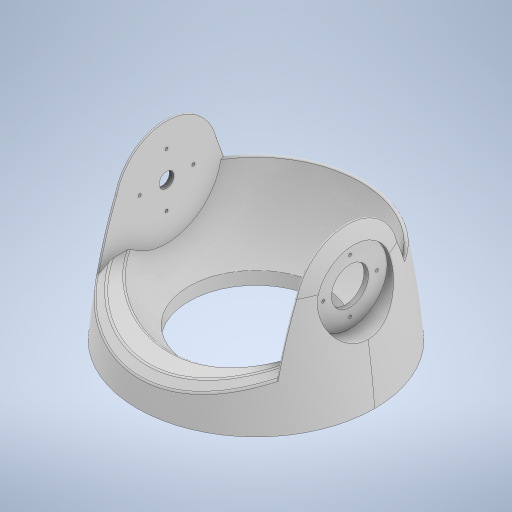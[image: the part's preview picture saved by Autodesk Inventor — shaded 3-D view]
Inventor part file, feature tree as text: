
AUTODESK INVENTOR PART (.ipt)
format: ipt  version: 2023 (Build 270158000, 158)  size: 764,416 bytes
history: native  units: mm
features: sketch x17, extrude x16, fillet x4, other x3, revolve x3, chamfer x3, mirror x2, projected_geometry x2, pattern_circular x1
ambient origin geometry x8: Origin, YZ Plane, XZ Plane, XY Plane, X Axis, Y Axis, Z Axis, Center Point
bodies: Body1 (feature_tree)
feature tree (51):
  other  "솔리드1"
  revolve  "회전1"
  sketch  "스케치2"
  revolve  "회전2"
  revolve  "회전3"
  extrude  "돌출3"  Depth=120.0mm
  extrude  "돌출4"  Depth=140.0mm
  chamfer  "모따기1"  Distance=60.0mm
  fillet  "모깎기1"  Radius=130.0mm
  extrude  "돌출5"  Depth=160.0mm
  fillet  "모깎기2"  [1 undecoded]
  fillet  "모깎기3"  Radius=120.0mm
  extrude  "돌출6"  Depth=141.0mm
  other  "작업 평면2"
  extrude  "돌출7"  TaperAngle=90.0deg  [1 undecoded]
  mirror  "미러1"
  extrude  "돌출9"  Depth=4.0mm
  extrude  "돌출10"  TaperAngle=90.0deg  [1 undecoded]
  mirror  "미러2"
  sketch  "스케치13"
  extrude  "돌출11"  Depth=10.0mm
  extrude  "돌출12"  Depth=371.75mm TaperAngle=0.0deg
  sketch  "스케치15"
  extrude  "돌출13"  Depth=25.0mm
  extrude  "돌출14"  Depth=140.0mm
  pattern_circular  "원형 패턴1"  [2 undecoded]
  extrude  "돌출15"  Depth=103.5mm TaperAngle=0.0deg
  fillet  "모깎기4"  Radius=5.0mm
  other  "작업 평면4"
  extrude  "돌출16"  Depth=2.0mm
  chamfer  "모따기2"  Distance=90.0mm
  extrude  "돌출17"  Depth=103.5mm TaperAngle=0.0deg
  chamfer  "모따기3"  Distance=1.0mm
  extrude  "돌출18"  Depth=0.5mm
  extrude  "돌출19"  Depth=7.0mm TaperAngle=0.0deg
  sketch  "스케치1"
  sketch  "스케치3"
  projected_geometry  "투영된 루프1"
  sketch  "스케치5"
  sketch  "스케치6"
  sketch  "스케치7"
  sketch  "스케치8"
  projected_geometry  "투영된 루프2"
  sketch  "스케치9"
  sketch  "스케치11"
  sketch  "스케치12"
  sketch  "스케치16"
  sketch  "스케치17"
  sketch  "스케치18"
  sketch  "스케치20"
  sketch  "스케치21"
note: 5 required parameter values undecoded (feature->parameter linkage not recoverable at this tier; creation-order binding heuristic only, values carry confidence <= 0.55)
